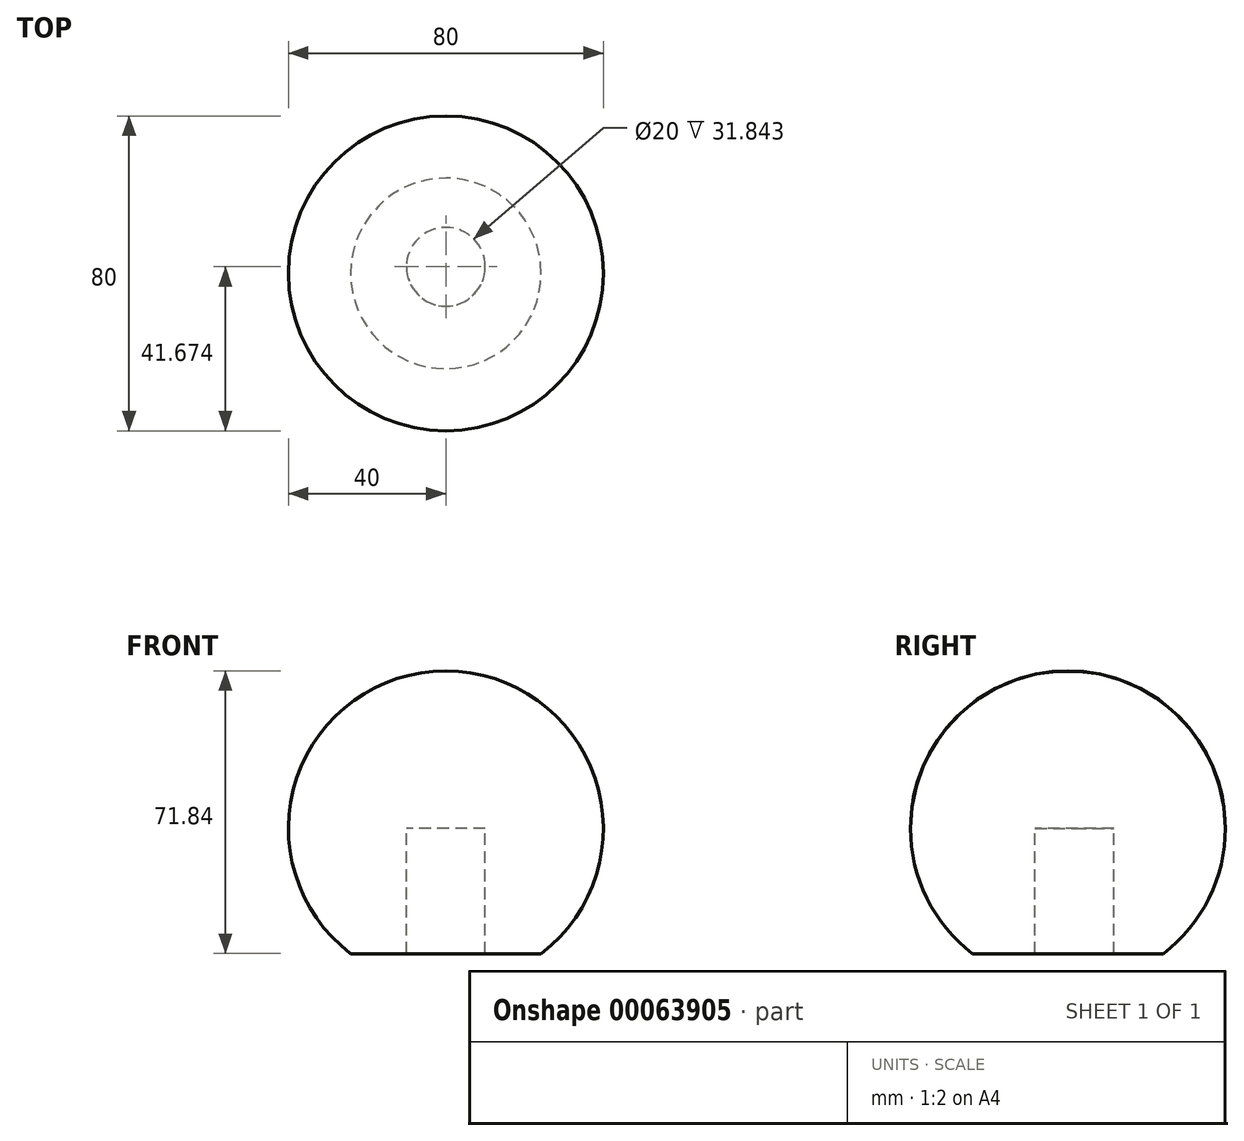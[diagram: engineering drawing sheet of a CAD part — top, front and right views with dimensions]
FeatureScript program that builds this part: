
annotation { "Feature Type Name" : "Feature", "Feature Type Description" : "" }
export const myFeature = defineFeature(function(context is Context, id is Id, definition is map)
    precondition{}
    {
        {
            var Q0;
            Q0=qCreatedBy(makeId("Right.planeOp"),FACE);
            var sketch = newSketch(context, id + "F0", { "sketchPlane" : qUnion([Q0])});
            skArc(sketch, "E0", {"start": v(36.8, 0) * mm, "mid": v(-3.2, 40) * mm, "end": v(-43.2, 0) * mm});
            skLineSegment(sketch, "E1", {"start": v(36.8, 0) * mm, "end": v(-43.2, 0) * mm});
            skSolve(sketch);
        }
        {
            var Q0;
            Q0=makeQuery(id+"F0.imprint","IMPRINT",FACE,{"disambiguationData":[TD([[makeQuery(id+"F0.imprint","IMPRINT",EDGE,{"derivedFrom":sQuery(id+"F0.wireOp",EDGE,"E0")}),1.0]])]});
            var Q1;
            Q1=sQuery(id+"F0.wireOp",EDGE,"E1");
            revolve(context, id + "F1", {"entities" : qUnion([Q0]), "axis" : qUnion([Q1]), "revolveType" : RevolveType.FULL});
        }
        {
            var Q0;
            Q0=qCreatedBy(makeId("Top.planeOp"),FACE);
            var sketch = newSketch(context, id + "F2", { "sketchPlane" : qUnion([Q0])});
            skCircle(sketch, "E2", {"center": v(0, -1.52) * mm, "radius": 10 * mm});
            skSolve(sketch);
        }
        {
            var Q0;
            Q0 = qSketchRegion(id + "F2", true);
            extrude(context, id + "F3", {"entities" : qUnion([Q0]), "operationType" : NewBodyOperationType.REMOVE, "endBound" : BoundingType.THROUGH_ALL, "oppositeDirection" : true, "depth" : 25 * mm});
        }
        {
            var Q0;
            Q0=qCreatedBy(makeId("Right.planeOp"),FACE);
            var sketch = newSketch(context, id + "F4", { "sketchPlane" : qUnion([Q0])});
            skLineSegment(sketch, "E3", {"start": v(-29.2, -31.84) * mm, "end": v(22.77, -31.84) * mm});
            skLineSegment(sketch, "E4", {"start": v(22.77, -31.84) * mm, "end": v(22.77, -53.3) * mm});
            skLineSegment(sketch, "E5", {"start": v(22.77, -53.3) * mm, "end": v(-29.2, -53.3) * mm});
            skLineSegment(sketch, "E6", {"start": v(-29.2, -53.3) * mm, "end": v(-29.2, -31.84) * mm});
            skSolve(sketch);
        }
        {
            var Q0;
            Q0=makeQuery(id+"F4.imprint","IMPRINT",FACE,{"disambiguationData":[TD([[makeQuery(id+"F4.imprint","IMPRINT",EDGE,{"derivedFrom":sQuery(id+"F4.wireOp",EDGE,"E3")}),-1.0]])]});
            extrude(context, id + "F5", {"entities" : qUnion([Q0]), "operationType" : NewBodyOperationType.REMOVE, "oppositeDirection" : true, "depth" : 35.64 * mm});
        }
        {
            var Q0;
            Q0 = qSketchRegion(id + "F4", true);
            extrude(context, id + "F6", {"entities" : qUnion([Q0]), "operationType" : NewBodyOperationType.REMOVE, "depth" : 33.2 * mm});
        }
    });
